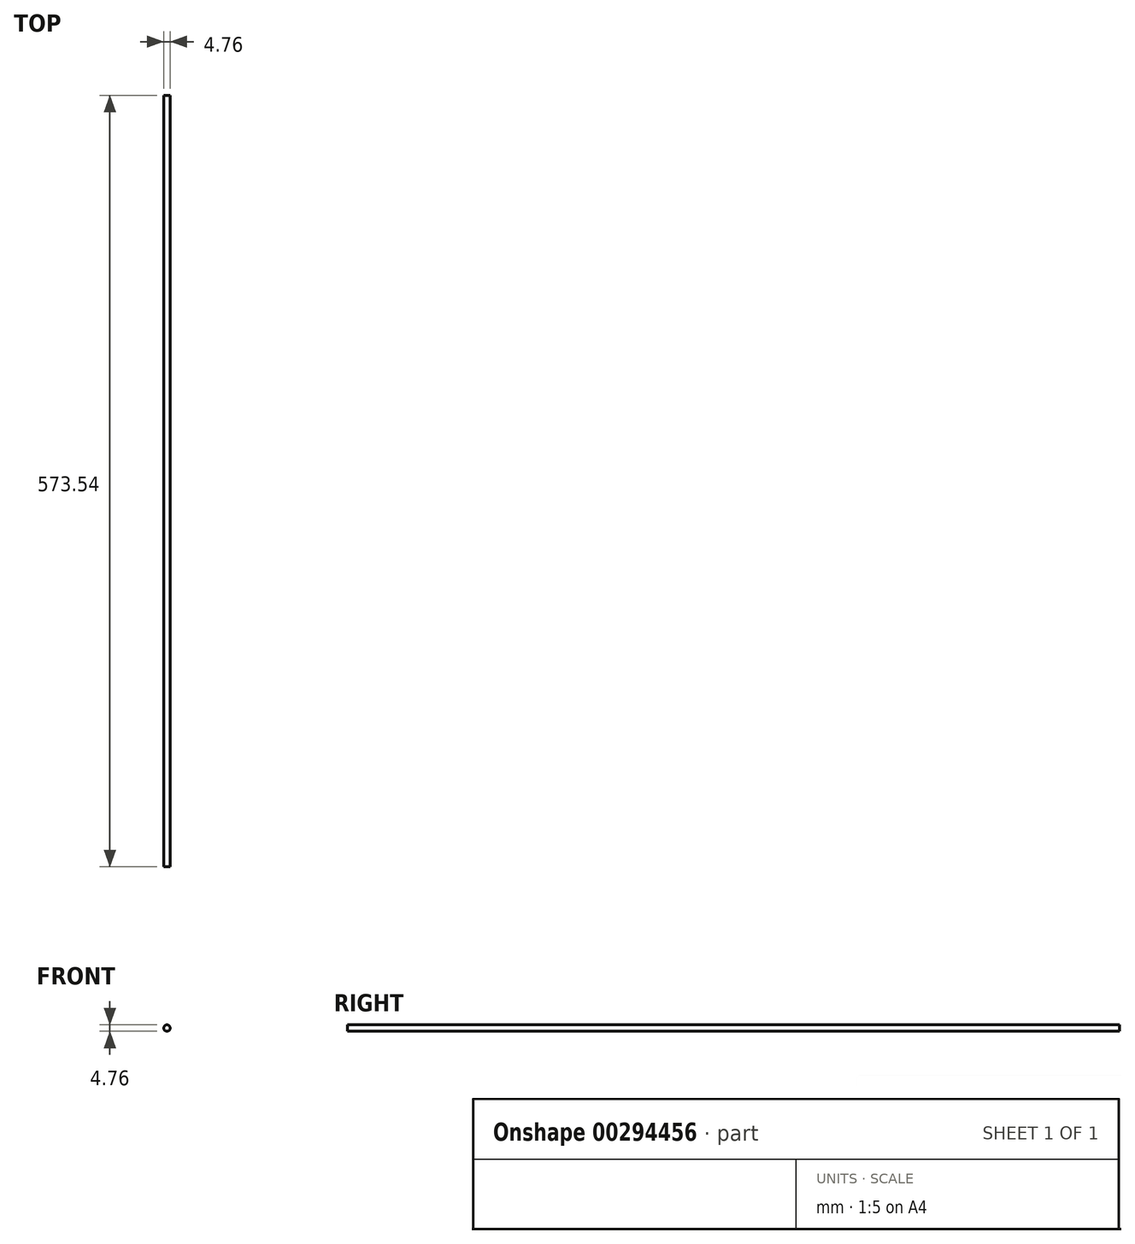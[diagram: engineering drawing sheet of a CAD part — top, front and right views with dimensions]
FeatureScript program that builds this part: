
annotation { "Feature Type Name" : "Feature", "Feature Type Description" : "" }
export const myFeature = defineFeature(function(context is Context, id is Id, definition is map)
    precondition{}
    {
        {
            var Q0;
            Q0=qCreatedBy(makeId("Front.planeOp"),FACE);
            var sketch = newSketch(context, id + "F0", { "sketchPlane" : qUnion([Q0])});
            skCircle(sketch, "E0", {"center": v(0, 0) * mm, "radius": 2.38 * mm});
            skSolve(sketch);
        }
        {
            var Q0;
            Q0=makeQuery(id+"F0.imprint","IMPRINT",FACE,{"disambiguationData":[TD([[makeQuery(id+"F0.imprint","IMPRINT",EDGE,{"derivedFrom":sQuery(id+"F0.wireOp",EDGE,"E0")}),1.0]])]});
            extrude(context, id + "F1", {"entities" : qUnion([Q0]), "endBound" : BoundingType.SYMMETRIC, "depth" : 573.53 * mm});
        }
    });
